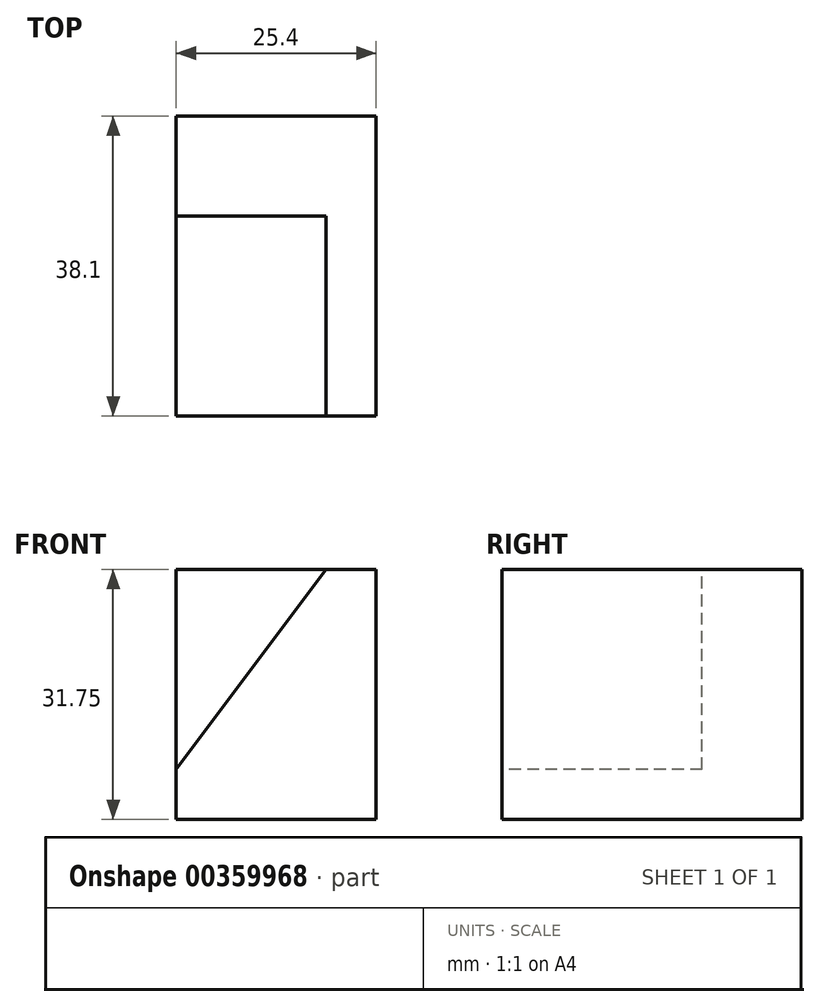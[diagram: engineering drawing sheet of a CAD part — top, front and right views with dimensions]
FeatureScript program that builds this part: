
annotation { "Feature Type Name" : "Feature", "Feature Type Description" : "" }
export const myFeature = defineFeature(function(context is Context, id is Id, definition is map)
    precondition{}
    {
        {
            var Q0;
            Q0=qCreatedBy(makeId("Right.planeOp"),FACE);
            var sketch = newSketch(context, id + "F0", { "sketchPlane" : qUnion([Q0])});
            skLineSegment(sketch, "E0", {"start": v(0, 31.75) * mm, "end": v(38.1, 31.75) * mm});
            skLineSegment(sketch, "E1", {"start": v(38.1, 31.75) * mm, "end": v(38.1, 0) * mm});
            skLineSegment(sketch, "E2", {"start": v(38.1, 0) * mm, "end": v(0, 0) * mm});
            skLineSegment(sketch, "E3", {"start": v(0, 0) * mm, "end": v(0, 31.75) * mm});
            skSolve(sketch);
        }
        {
            var Q0;
            Q0 = qSketchRegion(id + "F0", true);
            extrude(context, id + "F1", {"entities" : qUnion([Q0]), "depth" : 25.4 * mm});
        }
        {
            var Q0;
            Q0=qCreatedBy(makeId("Right.planeOp"),FACE);
            var sketch = newSketch(context, id + "F2", { "sketchPlane" : qUnion([Q0])});
            skLineSegment(sketch, "E4", {"start": v(8.05, 30.49) * mm, "end": v(8.05, 9.13) * mm});
            skLineSegment(sketch, "E5", {"start": v(8.05, 9.13) * mm, "end": v(34.36, 9.13) * mm});
            skLineSegment(sketch, "E6", {"start": v(8.05, 30.49) * mm, "end": v(21.05, 30.49) * mm});
            skLineSegment(sketch, "E7", {"start": v(21.05, 30.49) * mm, "end": v(8.05, 9.13) * mm});
            skLineSegment(sketch, "E8", {"start": v(9.9, 8.2) * mm, "end": v(8.05, 9.13) * mm});
            skLineSegment(sketch, "E9", {"start": v(34.36, 9.13) * mm, "end": v(34.36, 30.8) * mm});
            skLineSegment(sketch, "E10", {"start": v(34.36, 30.8) * mm, "end": v(21.05, 30.8) * mm});
            skSolve(sketch);
        }
        {
            var Q0;
            Q0 = qSketchRegion(id + "F2", true);
            extrude(context, id + "F3", {"entities" : qUnion([Q0]), "operationType" : NewBodyOperationType.ADD, "depth" : 15.75 * mm});
        }
        {
            var Q0;
            Q0=makeQuery(id+"F1.opExtrude","SWEPT_FACE",FACE,{"disambiguationData":[OSD([sQuery(id+"F0.wireOp",EDGE,"E3")])]});
            var sketch = newSketch(context, id + "F4", { "sketchPlane" : qUnion([Q0])});
            skLineSegment(sketch, "E11", {"start": v(19.05, 31.75) * mm, "end": v(0, 6.35) * mm});
            skSolve(sketch);
        }
        {
            var Q0;
            {var subQ0=sQuery(id+"F4.wireOp",EDGE,"E11");Q0=makeQuery(id+"F4.imprint","IMPRINT",FACE,{"disambiguationData":[TD([[makeQuery(id+"F4.imprint","IMPRINT",EDGE,{"derivedFrom":subQ0}),-1.0]])]});}
            extrude(context, id + "F5", {"entities" : qUnion([Q0]), "operationType" : NewBodyOperationType.REMOVE, "oppositeDirection" : true, "depth" : 25.4 * mm});
        }
    });
